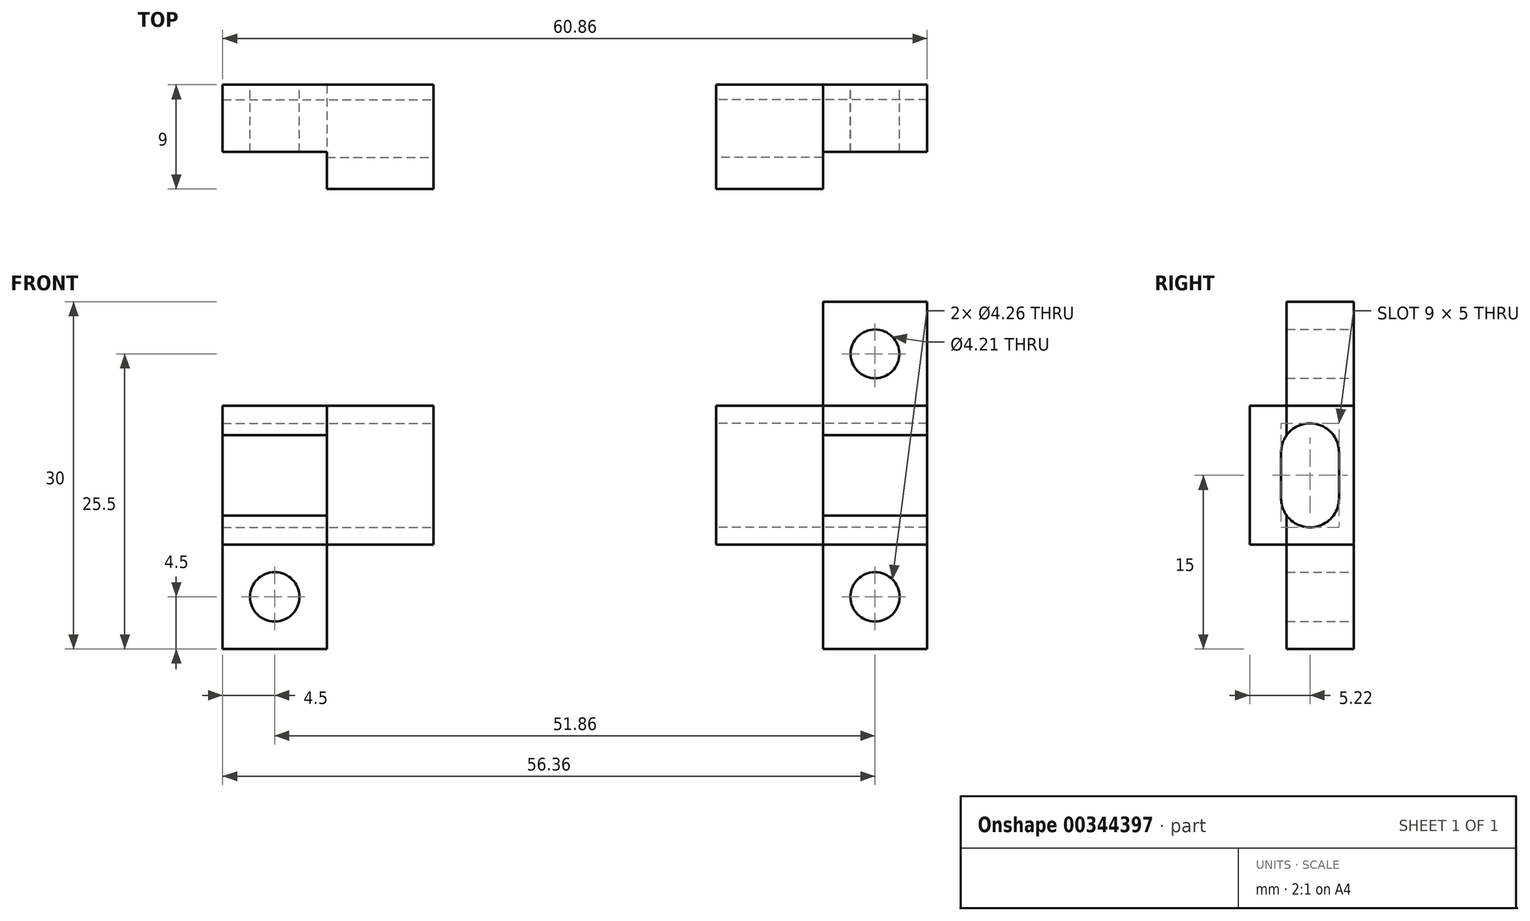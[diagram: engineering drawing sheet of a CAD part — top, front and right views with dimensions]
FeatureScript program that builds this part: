
annotation { "Feature Type Name" : "Feature", "Feature Type Description" : "" }
export const myFeature = defineFeature(function(context is Context, id is Id, definition is map)
    precondition{}
    {
        {
            var Q0;
            Q0=qCreatedBy(makeId("Top.planeOp"),FACE);
            var sketch = newSketch(context, id + "F0", { "sketchPlane" : qUnion([Q0])});
            skLineSegment(sketch, "E0.bottom", {"start": v(-21.43, 21.43) * mm, "end": v(21.43, 21.43) * mm});
            skLineSegment(sketch, "E0.top", {"start": v(-21.43, -21.43) * mm, "end": v(21.43, -21.43) * mm});
            skLineSegment(sketch, "E0.left", {"start": v(-21.43, 21.43) * mm, "end": v(-21.43, -21.43) * mm});
            skLineSegment(sketch, "E0.right", {"start": v(21.43, 21.43) * mm, "end": v(21.43, -21.43) * mm});
            skPoint(sketch, "E0.middle", {"position": v(0, 0) * mm});
            skLineSegment(sketch, "E1.bottom", {"start": v(-30.43, 30.43) * mm, "end": v(30.43, 30.43) * mm});
            skLineSegment(sketch, "E1.top", {"start": v(-30.43, -30.43) * mm, "end": v(30.43, -30.43) * mm});
            skLineSegment(sketch, "E1.left", {"start": v(-30.43, 30.43) * mm, "end": v(-30.43, -30.43) * mm});
            skLineSegment(sketch, "E1.right", {"start": v(30.43, 30.43) * mm, "end": v(30.43, -30.43) * mm});
            skPoint(sketch, "E2.oppositeSnap0", {"position": v(0, 21.43) * mm});
            skLineSegment(sketch, "E2.bottom", {"start": v(0, 21.43) * mm, "end": v(0, 21.43) * mm});
            skLineSegment(sketch, "E2.top", {"start": v(0, 30.43) * mm, "end": v(0, 30.43) * mm});
            skLineSegment(sketch, "E2.left", {"start": v(0, 21.43) * mm, "end": v(0, 30.43) * mm});
            skLineSegment(sketch, "E2.right", {"start": v(0, 21.43) * mm, "end": v(0, 30.43) * mm});
            skPoint(sketch, "E3.oppositeSnap0", {"position": v(21.43, 0) * mm});
            skLineSegment(sketch, "E3.bottom", {"start": v(21.43, 0) * mm, "end": v(30.43, 0) * mm});
            skLineSegment(sketch, "E3.top", {"start": v(21.43, 0) * mm, "end": v(30.43, 0) * mm});
            skLineSegment(sketch, "E3.left", {"start": v(21.43, 0) * mm, "end": v(21.43, 0) * mm});
            skLineSegment(sketch, "E3.right", {"start": v(30.43, 0) * mm, "end": v(30.43, 0) * mm});
            skLineSegment(sketch, "E4", {"start": v(0, -21.43) * mm, "end": v(0, -30.43) * mm});
            skLineSegment(sketch, "E5", {"start": v(12.2, -21.43) * mm, "end": v(12.2, -30.43) * mm});
            skLineSegment(sketch, "E6", {"start": v(-12.2, -21.43) * mm, "end": v(-12.2, -30.43) * mm});
            skLineSegment(sketch, "E7", {"start": v(-21.43, 0) * mm, "end": v(-30.43, 0) * mm});
            skLineSegment(sketch, "E8", {"start": v(21.43, -21.43) * mm, "end": v(30.43, -21.43) * mm});
            skLineSegment(sketch, "E9", {"start": v(-21.43, -21.43) * mm, "end": v(-30.43, -21.43) * mm});
            skLineSegment(sketch, "E10", {"start": v(21.43, -21.43) * mm, "end": v(21.43, -30.43) * mm});
            skLineSegment(sketch, "E11", {"start": v(-21.43, -21.43) * mm, "end": v(-21.43, -30.43) * mm});
            skLineSegment(sketch, "E12", {"start": v(30.43, -30.43) * mm, "end": v(30.43, -27.23) * mm});
            skLineSegment(sketch, "E13", {"start": v(30.43, -27.23) * mm, "end": v(21.43, -27.23) * mm});
            skLineSegment(sketch, "E14", {"start": v(-21.43, -30.43) * mm, "end": v(-21.43, -27.23) * mm});
            skLineSegment(sketch, "E15", {"start": v(-21.43, -27.23) * mm, "end": v(-30.43, -27.23) * mm});
            skSolve(sketch);
        }
        {
            var Q0;
            {var subQ0=sQuery(id+"F0.wireOp",EDGE,"E6");Q0=makeQuery(id+"F0.imprint","IMPRINT",FACE,{"disambiguationData":[TD([[makeQuery(id+"F0.imprint","IMPRINT",EDGE,{"derivedFrom":subQ0}),-1.0]])]});}
            var Q1;
            {var subQ4=sQuery(id+"F0.wireOp",EDGE,"E5");Q1=makeQuery(id+"F0.imprint","IMPRINT",FACE,{"disambiguationData":[TD([[makeQuery(id+"F0.imprint","IMPRINT",EDGE,{"derivedFrom":subQ4}),1.0]])]});}
            var Q2;
            {var subQ2=sQuery(id+"F0.wireOp",EDGE,"E8");Q2=makeQuery(id+"F0.imprint","IMPRINT",FACE,{"disambiguationData":[TD([[makeQuery(id+"F0.imprint","IMPRINT",EDGE,{"derivedFrom":subQ2}),-1.0]])]});}
            var Q3;
            {var subQ0=sQuery(id+"F0.wireOp",EDGE,"E12");Q3=makeQuery(id+"F0.imprint","IMPRINT",FACE,{"disambiguationData":[TD([[makeQuery(id+"F0.imprint","IMPRINT",EDGE,{"derivedFrom":subQ0}),1.0]])]});}
            var Q4;
            {var subQ0=sQuery(id+"F0.wireOp",EDGE,"E9");Q4=makeQuery(id+"F0.imprint","IMPRINT",FACE,{"disambiguationData":[TD([[makeQuery(id+"F0.imprint","IMPRINT",EDGE,{"derivedFrom":subQ0}),1.0]])]});}
            var Q5;
            {var subQ3=sQuery(id+"F0.wireOp",EDGE,"E14");Q5=makeQuery(id+"F0.imprint","IMPRINT",FACE,{"disambiguationData":[TD([[makeQuery(id+"F0.imprint","IMPRINT",EDGE,{"derivedFrom":subQ3}),1.0]])]});}
            extrude(context, id + "F1", {"entities" : qUnion([Q0, Q1, Q2, Q3, Q4, Q5]), "depth" : 12 * mm});
        }
        {
            var Q0;
            Q0=makeQuery(id+"F1.opExtrude","SWEPT_FACE",FACE,{"disambiguationData":[OSD([sQuery(id+"F0.wireOp",EDGE,"E5")])]});
            var sketch = newSketch(context, id + "F2", { "sketchPlane" : qUnion([Q0])});
            skLineSegment(sketch, "E16", {"start": v(21.43, 6) * mm, "end": v(22.71, 6) * mm});
            skLineSegment(sketch, "E17", {"start": v(22.71, 6) * mm, "end": v(25.21, 6) * mm});
            skCircle(sketch, "E18", {"center": v(25.21, 8) * mm, "radius": 2.5 * mm});
            skCircle(sketch, "E19", {"center": v(25.21, 4) * mm, "radius": 2.5 * mm});
            skLineSegment(sketch, "E20", {"start": v(22.71, 8) * mm, "end": v(22.71, 4) * mm});
            skLineSegment(sketch, "E21", {"start": v(22.71, 4) * mm, "end": v(27.7, 4) * mm});
            skLineSegment(sketch, "E22", {"start": v(27.7, 4) * mm, "end": v(27.7, 8) * mm});
            skLineSegment(sketch, "E23", {"start": v(27.7, 8) * mm, "end": v(25.21, 8) * mm});
            skLineSegment(sketch, "E24", {"start": v(22.71, 8) * mm, "end": v(25.21, 8) * mm});
            skLineSegment(sketch, "E25", {"start": v(27.7, 6) * mm, "end": v(30.43, 6) * mm});
            skSolve(sketch);
        }
        {
            var Q0;
            Q0=makeQuery(id+"F1.opExtrude","CAP_FACE",FACE,{"disambiguationData":[OSD([sQuery(id+"F0.wireOp",EDGE,"E0.top"),sQuery(id+"F0.wireOp",EDGE,"E1.top"),sQuery(id+"F0.wireOp",EDGE,"E1.right"),sQuery(id+"F0.wireOp",EDGE,"E5"),sQuery(id+"F0.wireOp",EDGE,"E8"),sQuery(id+"F0.wireOp",EDGE,"E12")])],"isStart":false});
            var sketch = newSketch(context, id + "F3", { "sketchPlane" : qUnion([Q0])});
            skLineSegment(sketch, "E26", {"start": v(30.43, -30.43) * mm, "end": v(30.43, -27.23) * mm});
            skLineSegment(sketch, "E27", {"start": v(30.43, -27.23) * mm, "end": v(21.43, -27.23) * mm});
            skLineSegment(sketch, "E28", {"start": v(21.43, -27.23) * mm, "end": v(21.43, -21.43) * mm});
            skLineSegment(sketch, "E29", {"start": v(21.43, -27.23) * mm, "end": v(21.43, -30.43) * mm});
            skSolve(sketch);
        }
        {
            var Q0;
            Q0=makeQuery(id+"F1.opExtrude","CAP_FACE",FACE,{"disambiguationData":[OSD([sQuery(id+"F0.wireOp",EDGE,"E0.top"),sQuery(id+"F0.wireOp",EDGE,"E1.top"),sQuery(id+"F0.wireOp",EDGE,"E1.left"),sQuery(id+"F0.wireOp",EDGE,"E6"),sQuery(id+"F0.wireOp",EDGE,"E9")])],"isStart":false});
            var sketch = newSketch(context, id + "F4", { "sketchPlane" : qUnion([Q0])});
            skLineSegment(sketch, "E30", {"start": v(-30.43, -30.43) * mm, "end": v(-30.43, -27.23) * mm});
            skLineSegment(sketch, "E31", {"start": v(-30.43, -27.23) * mm, "end": v(-21.43, -27.23) * mm});
            skLineSegment(sketch, "E32", {"start": v(-21.43, -27.23) * mm, "end": v(-21.43, -30.43) * mm});
            skLineSegment(sketch, "E33", {"start": v(-21.43, -27.23) * mm, "end": v(-21.43, -21.43) * mm});
            skSolve(sketch);
        }
        {
            var Q0;
            {var subQ2=sQuery(id+"F0.wireOp",EDGE,"E8");Q0=makeQuery(id+"F0.imprint","IMPRINT",FACE,{"disambiguationData":[TD([[makeQuery(id+"F0.imprint","IMPRINT",EDGE,{"derivedFrom":subQ2}),-1.0]])]});}
            var Q1;
            {var subQ0=sQuery(id+"F0.wireOp",EDGE,"E9");Q1=makeQuery(id+"F0.imprint","IMPRINT",FACE,{"disambiguationData":[TD([[makeQuery(id+"F0.imprint","IMPRINT",EDGE,{"derivedFrom":subQ0}),1.0]])]});}
            extrude(context, id + "F5", {"entities" : qUnion([Q0, Q1]), "oppositeDirection" : true, "depth" : 9 * mm});
        }
        {
            var Q0;
            {var subQ0=sQuery(id+"F3.wireOp",EDGE,"E27");Q0=makeQuery(id+"F3.imprint","IMPRINT",FACE,{"disambiguationData":[TD([[makeQuery(id+"F3.imprint","IMPRINT",EDGE,{"derivedFrom":subQ0}),-1.0]])]});}
            var Q1;
            {var subQ0=sQuery(id+"F4.wireOp",EDGE,"E31");Q1=makeQuery(id+"F4.imprint","IMPRINT",FACE,{"disambiguationData":[TD([[makeQuery(id+"F4.imprint","IMPRINT",EDGE,{"derivedFrom":subQ0}),1.0]])]});}
            extrude(context, id + "F6", {"entities" : qUnion([Q0, Q1]), "depth" : 9 * mm});
        }
        {
            var Q0;
            Q0=makeQuery(id+"F6.opExtrude","SWEPT_FACE",FACE,{"disambiguationData":[OSD([sQuery(id+"F0.wireOp",EDGE,"E0.top"),sQuery(id+"F0.wireOp",EDGE,"E9")])]});
            var sketch = newSketch(context, id + "F7", { "sketchPlane" : qUnion([Q0])});
            skLineSegment(sketch, "E34", {"start": v(25.93, 12) * mm, "end": v(25.93, 16.5) * mm});
            skCircle(sketch, "E35", {"center": v(25.93, 16.5) * mm, "radius": 2.13 * mm});
            skSolve(sketch);
        }
        {
            var Q0;
            Q0=makeQuery(id+"F7.imprint","IMPRINT",FACE,{"disambiguationData":[TD([[makeQuery(id+"F7.imprint","IMPRINT",EDGE,{"derivedFrom":sQuery(id+"F7.wireOp",EDGE,"E35")}),1.0]])]});
            extrude(context, id + "F8", {"entities" : qUnion([Q0]), "operationType" : NewBodyOperationType.REMOVE, "oppositeDirection" : true, "depth" : 25 * mm});
        }
        {
            var Q0;
            Q0=makeQuery(id+"F5.opExtrude","SWEPT_FACE",FACE,{"disambiguationData":[OSD([sQuery(id+"F0.wireOp",EDGE,"E9")])]});
            var sketch = newSketch(context, id + "F9", { "sketchPlane" : qUnion([Q0])});
            skLineSegment(sketch, "E36", {"start": v(25.93, 0) * mm, "end": v(25.93, -4.5) * mm});
            skCircle(sketch, "E37", {"center": v(25.93, -4.5) * mm, "radius": 2.13 * mm});
            skSolve(sketch);
        }
        {
            var Q0;
            Q0=makeQuery(id+"F9.imprint","IMPRINT",FACE,{"disambiguationData":[TD([[makeQuery(id+"F9.imprint","IMPRINT",EDGE,{"derivedFrom":sQuery(id+"F9.wireOp",EDGE,"E37")}),1.0]])]});
            extrude(context, id + "F10", {"entities" : qUnion([Q0]), "operationType" : NewBodyOperationType.REMOVE, "oppositeDirection" : true, "depth" : 25 * mm});
        }
        {
            var Q0;
            Q0=makeQuery(id+"F6.opExtrude","SWEPT_FACE",FACE,{"disambiguationData":[OSD([sQuery(id+"F0.wireOp",EDGE,"E0.top"),sQuery(id+"F0.wireOp",EDGE,"E8")])]});
            var sketch = newSketch(context, id + "F11", { "sketchPlane" : qUnion([Q0])});
            skLineSegment(sketch, "E38", {"start": v(-25.93, 12) * mm, "end": v(-25.93, 16.5) * mm});
            skCircle(sketch, "E39", {"center": v(-25.93, 16.5) * mm, "radius": 2.1 * mm});
            skSolve(sketch);
        }
        {
            var Q0;
            Q0=makeQuery(id+"F11.imprint","IMPRINT",FACE,{"disambiguationData":[TD([[makeQuery(id+"F11.imprint","IMPRINT",EDGE,{"derivedFrom":sQuery(id+"F11.wireOp",EDGE,"E39")}),1.0]])]});
            extrude(context, id + "F12", {"entities" : qUnion([Q0]), "operationType" : NewBodyOperationType.REMOVE, "oppositeDirection" : true, "depth" : 25 * mm});
        }
        {
            var Q0;
            Q0=makeQuery(id+"F5.opExtrude","SWEPT_FACE",FACE,{"disambiguationData":[OSD([sQuery(id+"F0.wireOp",EDGE,"E8")])]});
            var sketch = newSketch(context, id + "F13", { "sketchPlane" : qUnion([Q0])});
            skLineSegment(sketch, "E40", {"start": v(-25.93, 0) * mm, "end": v(-25.93, -4.5) * mm});
            skCircle(sketch, "E41", {"center": v(-25.93, -4.5) * mm, "radius": 2.13 * mm});
            skSolve(sketch);
        }
        {
            var Q0;
            Q0=makeQuery(id+"F13.imprint","IMPRINT",FACE,{"disambiguationData":[TD([[makeQuery(id+"F13.imprint","IMPRINT",EDGE,{"derivedFrom":sQuery(id+"F13.wireOp",EDGE,"E41")}),1.0]])]});
            extrude(context, id + "F14", {"entities" : qUnion([Q0]), "operationType" : NewBodyOperationType.REMOVE, "oppositeDirection" : true, "depth" : 25 * mm});
        }
        {
            var Q0;
            {var subQ2=sQuery(id+"F2.wireOp",EDGE,"E23");Q0=makeQuery(id+"F2.imprint","IMPRINT",FACE,{"disambiguationData":[TD([[makeQuery(id+"F2.imprint","IMPRINT",EDGE,{"derivedFrom":subQ2}),-1.0]])]});}
            var Q1;
            {var subQ0=sQuery(id+"F2.wireOp",EDGE,"E23");Q1=makeQuery(id+"F2.imprint","IMPRINT",FACE,{"disambiguationData":[TD([[makeQuery(id+"F2.imprint","IMPRINT",EDGE,{"derivedFrom":subQ0}),1.0]])]});}
            var Q2;
            {var subQ0=sQuery(id+"F2.wireOp",EDGE,"E19");var subQ1=sQuery(id+"F2.wireOp",EDGE,"E18");var subQ2=makeQuery(id+"F2.imprint","INTERSECT",VERTEX,{"derivedFrom":[subQ1,subQ0]});Q2=makeQuery(id+"F2.imprint","IMPRINT",FACE,{"disambiguationData":[TD([[makeQuery(id+"F2.imprint","IMPRINT",EDGE,{"disambiguationData":[TD([[subQ2,1.0]])],"derivedFrom":subQ1}),1.0]])]});}
            var Q3;
            {var subQ0=sQuery(id+"F2.wireOp",EDGE,"E20");var subQ1=sQuery(id+"F2.wireOp",EDGE,"E17");var subQ2=makeQuery(id+"F2.imprint","INTERSECT",VERTEX,{"derivedFrom":[subQ1,subQ0]});Q3=makeQuery(id+"F2.imprint","IMPRINT",FACE,{"disambiguationData":[TD([[makeQuery(id+"F2.imprint","IMPRINT",EDGE,{"disambiguationData":[TD([[subQ2,-1.0]])],"derivedFrom":subQ1}),1.0]])]});}
            var Q4;
            {var subQ0=sQuery(id+"F2.wireOp",EDGE,"E20");var subQ1=sQuery(id+"F2.wireOp",EDGE,"E17");var subQ2=makeQuery(id+"F2.imprint","INTERSECT",VERTEX,{"derivedFrom":[subQ1,subQ0]});Q4=makeQuery(id+"F2.imprint","IMPRINT",FACE,{"disambiguationData":[TD([[makeQuery(id+"F2.imprint","IMPRINT",EDGE,{"disambiguationData":[TD([[subQ2,-1.0]])],"derivedFrom":subQ1}),-1.0]])]});}
            var Q5;
            {var subQ4=sQuery(id+"F2.wireOp",EDGE,"E21");Q5=makeQuery(id+"F2.imprint","IMPRINT",FACE,{"disambiguationData":[TD([[makeQuery(id+"F2.imprint","IMPRINT",EDGE,{"derivedFrom":subQ4}),1.0]])]});}
            var Q6;
            {var subQ0=sQuery(id+"F2.wireOp",EDGE,"E22");Q6=makeQuery(id+"F2.imprint","IMPRINT",FACE,{"disambiguationData":[TD([[makeQuery(id+"F2.imprint","IMPRINT",EDGE,{"derivedFrom":subQ0}),1.0]])]});}
            var Q7;
            {var subQ0=sQuery(id+"F2.wireOp",EDGE,"E21");Q7=makeQuery(id+"F2.imprint","IMPRINT",FACE,{"disambiguationData":[TD([[makeQuery(id+"F2.imprint","IMPRINT",EDGE,{"derivedFrom":subQ0}),-1.0]])]});}
            extrude(context, id + "F15", {"entities" : qUnion([Q0, Q1, Q2, Q3, Q4, Q5, Q6, Q7]), "operationType" : NewBodyOperationType.REMOVE, "oppositeDirection" : true, "depth" : 25 * mm});
        }
        {
            var Q0;
            {var subQ2=sQuery(id+"F2.wireOp",EDGE,"E23");Q0=makeQuery(id+"F2.imprint","IMPRINT",FACE,{"disambiguationData":[TD([[makeQuery(id+"F2.imprint","IMPRINT",EDGE,{"derivedFrom":subQ2}),-1.0]])]});}
            var Q1;
            {var subQ0=sQuery(id+"F2.wireOp",EDGE,"E23");Q1=makeQuery(id+"F2.imprint","IMPRINT",FACE,{"disambiguationData":[TD([[makeQuery(id+"F2.imprint","IMPRINT",EDGE,{"derivedFrom":subQ0}),1.0]])]});}
            var Q2;
            {var subQ0=sQuery(id+"F2.wireOp",EDGE,"E19");var subQ1=sQuery(id+"F2.wireOp",EDGE,"E18");var subQ2=makeQuery(id+"F2.imprint","INTERSECT",VERTEX,{"derivedFrom":[subQ1,subQ0]});Q2=makeQuery(id+"F2.imprint","IMPRINT",FACE,{"disambiguationData":[TD([[makeQuery(id+"F2.imprint","IMPRINT",EDGE,{"disambiguationData":[TD([[subQ2,1.0]])],"derivedFrom":subQ1}),1.0]])]});}
            var Q3;
            {var subQ4=sQuery(id+"F2.wireOp",EDGE,"E21");Q3=makeQuery(id+"F2.imprint","IMPRINT",FACE,{"disambiguationData":[TD([[makeQuery(id+"F2.imprint","IMPRINT",EDGE,{"derivedFrom":subQ4}),1.0]])]});}
            var Q4;
            {var subQ0=sQuery(id+"F2.wireOp",EDGE,"E20");var subQ1=sQuery(id+"F2.wireOp",EDGE,"E17");var subQ2=makeQuery(id+"F2.imprint","INTERSECT",VERTEX,{"derivedFrom":[subQ1,subQ0]});Q4=makeQuery(id+"F2.imprint","IMPRINT",FACE,{"disambiguationData":[TD([[makeQuery(id+"F2.imprint","IMPRINT",EDGE,{"disambiguationData":[TD([[subQ2,-1.0]])],"derivedFrom":subQ1}),1.0]])]});}
            var Q5;
            {var subQ0=sQuery(id+"F2.wireOp",EDGE,"E20");var subQ1=sQuery(id+"F2.wireOp",EDGE,"E17");var subQ2=makeQuery(id+"F2.imprint","INTERSECT",VERTEX,{"derivedFrom":[subQ1,subQ0]});Q5=makeQuery(id+"F2.imprint","IMPRINT",FACE,{"disambiguationData":[TD([[makeQuery(id+"F2.imprint","IMPRINT",EDGE,{"disambiguationData":[TD([[subQ2,-1.0]])],"derivedFrom":subQ1}),-1.0]])]});}
            var Q6;
            {var subQ0=sQuery(id+"F2.wireOp",EDGE,"E22");Q6=makeQuery(id+"F2.imprint","IMPRINT",FACE,{"disambiguationData":[TD([[makeQuery(id+"F2.imprint","IMPRINT",EDGE,{"derivedFrom":subQ0}),1.0]])]});}
            var Q7;
            {var subQ0=sQuery(id+"F2.wireOp",EDGE,"E21");Q7=makeQuery(id+"F2.imprint","IMPRINT",FACE,{"disambiguationData":[TD([[makeQuery(id+"F2.imprint","IMPRINT",EDGE,{"derivedFrom":subQ0}),-1.0]])]});}
            extrude(context, id + "F16", {"entities" : qUnion([Q0, Q1, Q2, Q3, Q4, Q5, Q6, Q7]), "operationType" : NewBodyOperationType.REMOVE, "depth" : 59 * mm});
        }
    });
